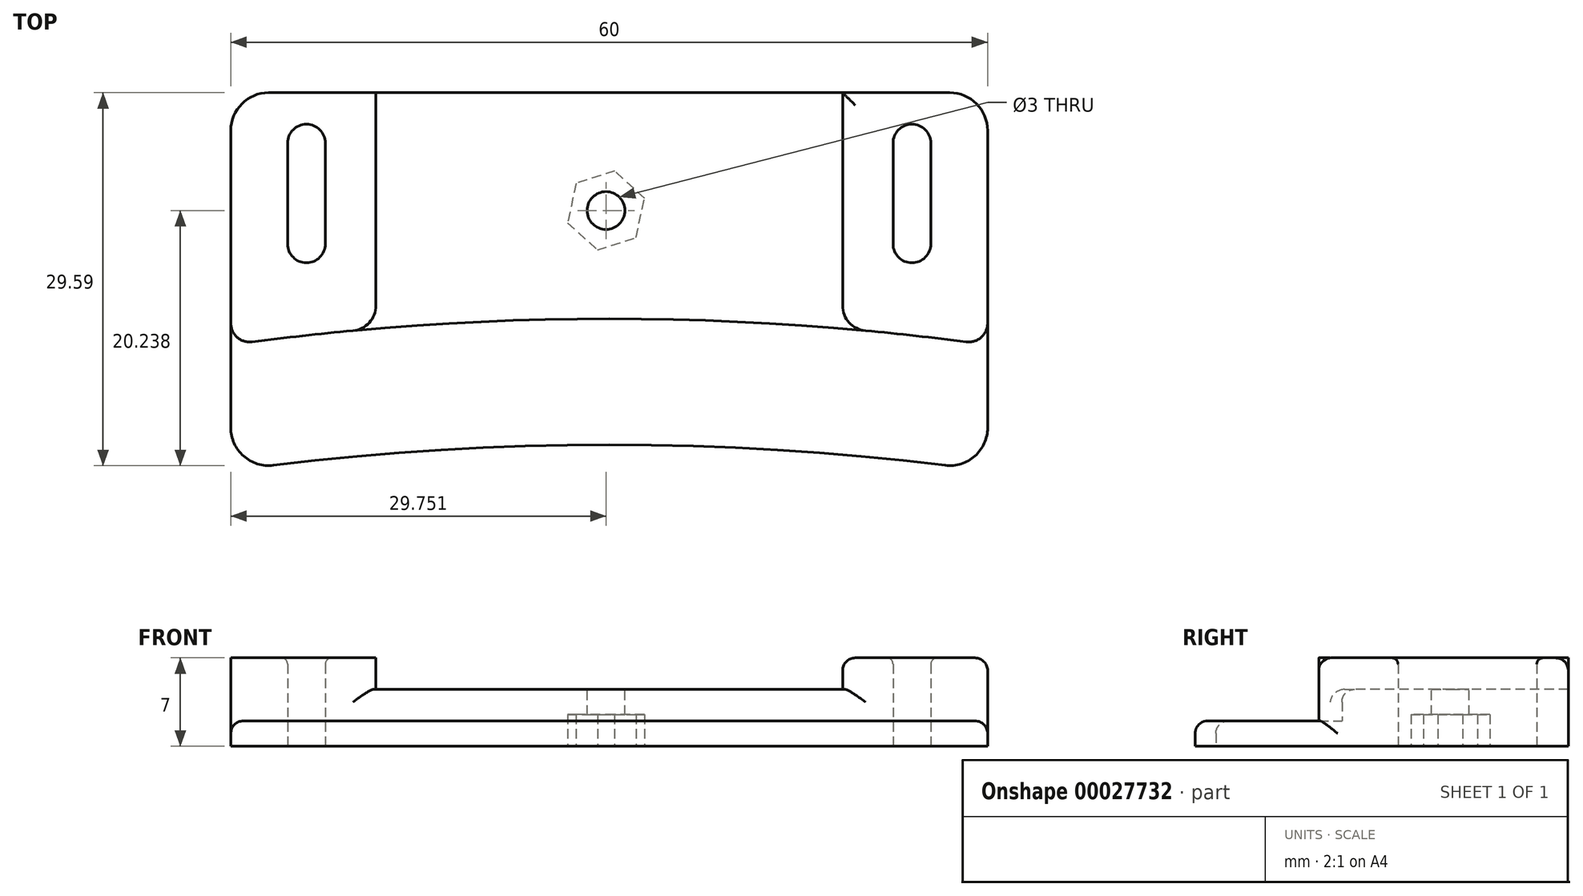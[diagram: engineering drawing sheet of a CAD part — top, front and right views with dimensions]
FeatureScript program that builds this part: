
annotation { "Feature Type Name" : "Feature", "Feature Type Description" : "" }
export const myFeature = defineFeature(function(context is Context, id is Id, definition is map)
    precondition{}
    {
        {
            var Q0;
            Q0=qCreatedBy(makeId("Top.planeOp"),FACE);
            var sketch = newSketch(context, id + "F0", { "sketchPlane" : qUnion([Q0])});
            skLineSegment(sketch, "E0.bottom", {"start": v(-20.27, 13.5) * mm, "end": v(33.73, 13.5) * mm});
            skLineSegment(sketch, "E0.left", {"start": v(-23.27, 10.5) * mm, "end": v(-23.27, -13.09) * mm});
            skLineSegment(sketch, "E0.right", {"start": v(36.73, 10.5) * mm, "end": v(36.73, -13.09) * mm});
            skLineSegment(sketch, "E1.bottom", {"start": v(-17.27, 11) * mm, "end": v(-17.27, 11) * mm});
            skLineSegment(sketch, "E1.top", {"start": v(-17.27, 0) * mm, "end": v(-17.27, 0) * mm});
            skLineSegment(sketch, "E1.left", {"start": v(-18.77, 9.5) * mm, "end": v(-18.77, 1.5) * mm});
            skLineSegment(sketch, "E1.right", {"start": v(-15.77, 9.5) * mm, "end": v(-15.77, 1.5) * mm});
            skLineSegment(sketch, "E2.bottom", {"start": v(30.73, 11) * mm, "end": v(30.73, 11) * mm});
            skLineSegment(sketch, "E2.top", {"start": v(30.73, 0) * mm, "end": v(30.73, 0) * mm});
            skLineSegment(sketch, "E2.left", {"start": v(29.23, 9.5) * mm, "end": v(29.23, 1.5) * mm});
            skLineSegment(sketch, "E2.right", {"start": v(32.23, 9.5) * mm, "end": v(32.23, 1.5) * mm});
            skArc(sketch, "E3", {"start": v(33.37, -16.06) * mm, "mid": v(6.73, -14.44) * mm, "end": v(-19.9, -16.06) * mm});
            skPoint(sketch, "E4.visualSharp", {"position": v(-23.27, 13.5) * mm});
            skArc(sketch, "E4.filletArc", {"start": v(-20.27, 13.5) * mm, "mid": v(-22.4, 12.62) * mm, "end": v(-23.27, 10.5) * mm});
            skPoint(sketch, "E5.visualSharp", {"position": v(-23.27, -16.5) * mm});
            skArc(sketch, "E5.filletArc", {"start": v(-23.27, -13.09) * mm, "mid": v(-22.26, -15.33) * mm, "end": v(-19.9, -16.06) * mm});
            skPoint(sketch, "E6.visualSharp", {"position": v(36.73, -16.5) * mm});
            skArc(sketch, "E6.filletArc", {"start": v(33.37, -16.06) * mm, "mid": v(35.72, -15.33) * mm, "end": v(36.73, -13.09) * mm});
            skPoint(sketch, "E7.visualSharp", {"position": v(36.73, 13.5) * mm});
            skArc(sketch, "E7.filletArc", {"start": v(36.73, 10.5) * mm, "mid": v(35.85, 12.62) * mm, "end": v(33.73, 13.5) * mm});
            skPoint(sketch, "E8.visualSharp", {"position": v(-18.77, 11) * mm});
            skArc(sketch, "E8.filletArc", {"start": v(-17.27, 11) * mm, "mid": v(-18.33, 10.56) * mm, "end": v(-18.77, 9.5) * mm});
            skPoint(sketch, "E9.visualSharp", {"position": v(-15.77, 11) * mm});
            skArc(sketch, "E9.filletArc", {"start": v(-15.77, 9.5) * mm, "mid": v(-16.2, 10.56) * mm, "end": v(-17.27, 11) * mm});
            skPoint(sketch, "E10.visualSharp", {"position": v(-18.77, 0) * mm});
            skArc(sketch, "E10.filletArc", {"start": v(-18.77, 1.5) * mm, "mid": v(-18.33, 0.44) * mm, "end": v(-17.27, 0) * mm});
            skPoint(sketch, "E11.visualSharp", {"position": v(-15.77, 0) * mm});
            skArc(sketch, "E11.filletArc", {"start": v(-17.27, 0) * mm, "mid": v(-16.2, 0.44) * mm, "end": v(-15.77, 1.5) * mm});
            skPoint(sketch, "E12.visualSharp", {"position": v(29.23, 0) * mm});
            skArc(sketch, "E12.filletArc", {"start": v(29.23, 1.5) * mm, "mid": v(29.67, 0.44) * mm, "end": v(30.73, 0) * mm});
            skPoint(sketch, "E13.visualSharp", {"position": v(32.23, 0) * mm});
            skArc(sketch, "E13.filletArc", {"start": v(30.73, 0) * mm, "mid": v(31.8, 0.44) * mm, "end": v(32.23, 1.5) * mm});
            skPoint(sketch, "E14.visualSharp", {"position": v(29.23, 11) * mm});
            skArc(sketch, "E14.filletArc", {"start": v(30.73, 11) * mm, "mid": v(29.67, 10.56) * mm, "end": v(29.23, 9.5) * mm});
            skPoint(sketch, "E15.visualSharp", {"position": v(32.23, 11) * mm});
            skArc(sketch, "E15.filletArc", {"start": v(32.23, 9.5) * mm, "mid": v(31.8, 10.56) * mm, "end": v(30.73, 11) * mm});
            skSolve(sketch);
        }
        {
            var Q0;
            Q0 = qSketchRegion(id + "F0", true);
            extrude(context, id + "F1", {"entities" : qUnion([Q0]), "depth" : 2 * mm});
        }
        {
            var Q0;
            Q0=makeQuery(id+"F1.opExtrude","CAP_FACE",FACE,{"disambiguationData":[OSD([sQuery(id+"F0.wireOp",EDGE,"E0.bottom"),sQuery(id+"F0.wireOp",EDGE,"E0.left"),sQuery(id+"F0.wireOp",EDGE,"E0.right"),sQuery(id+"F0.wireOp",EDGE,"E1.bottom"),sQuery(id+"F0.wireOp",EDGE,"E1.top"),sQuery(id+"F0.wireOp",EDGE,"E1.left"),sQuery(id+"F0.wireOp",EDGE,"E1.right"),sQuery(id+"F0.wireOp",EDGE,"E2.bottom"),sQuery(id+"F0.wireOp",EDGE,"E2.top"),sQuery(id+"F0.wireOp",EDGE,"E2.left"),sQuery(id+"F0.wireOp",EDGE,"E2.right"),sQuery(id+"F0.wireOp",EDGE,"E3"),sQuery(id+"F0.wireOp",EDGE,"E4.filletArc"),sQuery(id+"F0.wireOp",EDGE,"E5.filletArc"),sQuery(id+"F0.wireOp",EDGE,"E6.filletArc"),sQuery(id+"F0.wireOp",EDGE,"E7.filletArc"),sQuery(id+"F0.wireOp",EDGE,"E8.filletArc"),sQuery(id+"F0.wireOp",EDGE,"E9.filletArc"),sQuery(id+"F0.wireOp",EDGE,"E10.filletArc"),sQuery(id+"F0.wireOp",EDGE,"E11.filletArc"),sQuery(id+"F0.wireOp",EDGE,"E12.filletArc"),sQuery(id+"F0.wireOp",EDGE,"E13.filletArc"),sQuery(id+"F0.wireOp",EDGE,"E14.filletArc"),sQuery(id+"F0.wireOp",EDGE,"E15.filletArc")])],"isStart":false});
            var sketch = newSketch(context, id + "F2", { "sketchPlane" : qUnion([Q0])});
            skLineSegment(sketch, "E16", {"start": v(-23.27, -4.79) * mm, "end": v(-23.27, 10.5) * mm});
            skLineSegment(sketch, "E17", {"start": v(-20.27, 13.5) * mm, "end": v(33.73, 13.5) * mm});
            skLineSegment(sketch, "E18", {"start": v(36.73, 10.5) * mm, "end": v(36.73, -4.79) * mm});
            skArc(sketch, "E19", {"start": v(35.04, -6.27) * mm, "mid": v(6.73, -4.44) * mm, "end": v(-21.58, -6.27) * mm});
            skPoint(sketch, "E20.visualSharp", {"position": v(-23.27, -6.5) * mm});
            skArc(sketch, "E20.filletArc", {"start": v(-23.27, -4.79) * mm, "mid": v(-22.76, -5.91) * mm, "end": v(-21.58, -6.27) * mm});
            skPoint(sketch, "E21.visualSharp", {"position": v(36.73, -6.5) * mm});
            skArc(sketch, "E21.filletArc", {"start": v(35.04, -6.27) * mm, "mid": v(36.22, -5.91) * mm, "end": v(36.73, -4.79) * mm});
            skPoint(sketch, "E22.visualSharp", {"position": v(-23.27, 13.5) * mm});
            skArc(sketch, "E22.filletArc", {"start": v(-20.27, 13.5) * mm, "mid": v(-22.4, 12.62) * mm, "end": v(-23.27, 10.5) * mm});
            skPoint(sketch, "E23.visualSharp", {"position": v(36.73, 13.5) * mm});
            skArc(sketch, "E23.filletArc", {"start": v(36.73, 10.5) * mm, "mid": v(35.85, 12.62) * mm, "end": v(33.73, 13.5) * mm});
            skSolve(sketch);
        }
        {
            var Q0;
            Q0=makeQuery(id+"F2.imprint","IMPRINT",FACE,{"disambiguationData":[TD([[makeQuery(id+"F2.imprint","IMPRINT",EDGE,{"derivedFrom":sQuery(id+"F2.wireOp",EDGE,"E16")}),1.0]])]});
            extrude(context, id + "F3", {"entities" : qUnion([Q0]), "operationType" : NewBodyOperationType.ADD, "depth" : 5 * mm});
        }
        {
            var Q0;
            Q0=makeQuery(id+"F3.opExtrude","CAP_FACE",FACE,{"disambiguationData":[OSD([sQuery(id+"F0.wireOp",EDGE,"E1.bottom"),sQuery(id+"F0.wireOp",EDGE,"E1.top"),sQuery(id+"F0.wireOp",EDGE,"E1.left"),sQuery(id+"F0.wireOp",EDGE,"E1.right"),sQuery(id+"F0.wireOp",EDGE,"E2.bottom"),sQuery(id+"F0.wireOp",EDGE,"E2.top"),sQuery(id+"F0.wireOp",EDGE,"E2.left"),sQuery(id+"F0.wireOp",EDGE,"E2.right"),sQuery(id+"F0.wireOp",EDGE,"E8.filletArc"),sQuery(id+"F0.wireOp",EDGE,"E9.filletArc"),sQuery(id+"F0.wireOp",EDGE,"E10.filletArc"),sQuery(id+"F0.wireOp",EDGE,"E11.filletArc"),sQuery(id+"F0.wireOp",EDGE,"E12.filletArc"),sQuery(id+"F0.wireOp",EDGE,"E13.filletArc"),sQuery(id+"F0.wireOp",EDGE,"E14.filletArc"),sQuery(id+"F0.wireOp",EDGE,"E15.filletArc"),sQuery(id+"F2.wireOp",EDGE,"E16"),sQuery(id+"F2.wireOp",EDGE,"E17"),sQuery(id+"F2.wireOp",EDGE,"E18"),sQuery(id+"F2.wireOp",EDGE,"E19"),sQuery(id+"F2.wireOp",EDGE,"E20.filletArc"),sQuery(id+"F2.wireOp",EDGE,"E21.filletArc"),sQuery(id+"F2.wireOp",EDGE,"E22.filletArc"),sQuery(id+"F2.wireOp",EDGE,"E23.filletArc")])],"isStart":false});
            var sketch = newSketch(context, id + "F4", { "sketchPlane" : qUnion([Q0])});
            skLineSegment(sketch, "E24.bottom", {"start": v(-11.77, 13.5) * mm, "end": v(25.23, 13.5) * mm});
            skLineSegment(sketch, "E24.top", {"start": v(-11.77, -11.2) * mm, "end": v(25.23, -11.2) * mm});
            skLineSegment(sketch, "E24.left", {"start": v(-11.77, 13.5) * mm, "end": v(-11.77, -11.2) * mm});
            skLineSegment(sketch, "E24.right", {"start": v(25.23, 13.5) * mm, "end": v(25.23, -11.2) * mm});
            skSolve(sketch);
        }
        {
            var Q0;
            {var subQ6=sQuery(id+"F4.wireOp",EDGE,"E24.bottom");Q0=makeQuery(id+"F4.imprint","IMPRINT",FACE,{"disambiguationData":[TD([[makeQuery(id+"F4.imprint","IMPRINT",EDGE,{"derivedFrom":subQ6}),-1.0]])]});}
            var Q1;
            {var subQ5=sQuery(id+"F4.wireOp",EDGE,"E24.top");Q1=makeQuery(id+"F4.imprint","IMPRINT",FACE,{"disambiguationData":[TD([[makeQuery(id+"F4.imprint","IMPRINT",EDGE,{"derivedFrom":subQ5}),1.0]])]});}
            extrude(context, id + "F5", {"entities" : qUnion([Q0, Q1]), "operationType" : NewBodyOperationType.REMOVE, "oppositeDirection" : true, "depth" : 2.5 * mm});
        }
        {
            var Q0;
            Q0=makeQuery(id+"F5.boolean.opBoolean","COPY",FACE,{"derivedFrom":makeQuery(id+"F5.opExtrude","CAP_FACE",FACE,{"disambiguationData":[OSD([sQuery(id+"F4.wireOp",EDGE,"E24.bottom"),sQuery(id+"F4.wireOp",EDGE,"E24.top"),sQuery(id+"F4.wireOp",EDGE,"E24.left"),sQuery(id+"F4.wireOp",EDGE,"E24.right")])],"isStart":false})});
            var sketch = newSketch(context, id + "F6", { "sketchPlane" : qUnion([Q0])});
            skCircle(sketch, "E25", {"center": v(6.48, 4.15) * mm, "radius": 1.5 * mm});
            skSolve(sketch);
        }
        {
            var Q0;
            Q0 = qSketchRegion(id + "F6", true);
            extrude(context, id + "F7", {"entities" : qUnion([Q0]), "operationType" : NewBodyOperationType.REMOVE, "oppositeDirection" : true, "depth" : 25 * mm});
        }
        {
            var Q0;
            Q0=makeQuery(id+"F1.opExtrude","CAP_FACE",FACE,{"disambiguationData":[OSD([sQuery(id+"F0.wireOp",EDGE,"E0.bottom"),sQuery(id+"F0.wireOp",EDGE,"E0.left"),sQuery(id+"F0.wireOp",EDGE,"E0.right"),sQuery(id+"F0.wireOp",EDGE,"E1.bottom"),sQuery(id+"F0.wireOp",EDGE,"E1.top"),sQuery(id+"F0.wireOp",EDGE,"E1.left"),sQuery(id+"F0.wireOp",EDGE,"E1.right"),sQuery(id+"F0.wireOp",EDGE,"E2.bottom"),sQuery(id+"F0.wireOp",EDGE,"E2.top"),sQuery(id+"F0.wireOp",EDGE,"E2.left"),sQuery(id+"F0.wireOp",EDGE,"E2.right"),sQuery(id+"F0.wireOp",EDGE,"E3"),sQuery(id+"F0.wireOp",EDGE,"E4.filletArc"),sQuery(id+"F0.wireOp",EDGE,"E5.filletArc"),sQuery(id+"F0.wireOp",EDGE,"E6.filletArc"),sQuery(id+"F0.wireOp",EDGE,"E7.filletArc"),sQuery(id+"F0.wireOp",EDGE,"E8.filletArc"),sQuery(id+"F0.wireOp",EDGE,"E9.filletArc"),sQuery(id+"F0.wireOp",EDGE,"E10.filletArc"),sQuery(id+"F0.wireOp",EDGE,"E11.filletArc"),sQuery(id+"F0.wireOp",EDGE,"E12.filletArc"),sQuery(id+"F0.wireOp",EDGE,"E13.filletArc"),sQuery(id+"F0.wireOp",EDGE,"E14.filletArc"),sQuery(id+"F0.wireOp",EDGE,"E15.filletArc")])],"isStart":true});
            var sketch = newSketch(context, id + "F8", { "sketchPlane" : qUnion([Q0])});
            skCircle(sketch, "E26.cCircle", {"center": v(6.48, -4.15) * mm, "radius": 3.2 * mm, "construction": true});
            skLineSegment(sketch, "E26.0", {"start": v(9.53, -5.13) * mm, "end": v(7.15, -7.28) * mm});
            skLineSegment(sketch, "E26.1", {"start": v(7.15, -7.28) * mm, "end": v(4.1, -6.3) * mm});
            skLineSegment(sketch, "E26.2", {"start": v(4.1, -6.3) * mm, "end": v(3.43, -3.17) * mm});
            skLineSegment(sketch, "E26.3", {"start": v(3.43, -3.17) * mm, "end": v(5.8, -1.02) * mm});
            skLineSegment(sketch, "E26.4", {"start": v(5.8, -1.02) * mm, "end": v(8.86, -2) * mm});
            skLineSegment(sketch, "E26.5", {"start": v(8.86, -2) * mm, "end": v(9.53, -5.13) * mm});
            skSolve(sketch);
        }
        {
            var Q0;
            Q0 = qSketchRegion(id + "F8", true);
            extrude(context, id + "F9", {"entities" : qUnion([Q0]), "operationType" : NewBodyOperationType.REMOVE, "oppositeDirection" : true, "depth" : 2.5 * mm});
        }
        {
            var Q0;
            Q0=makeQuery(id+"F5.boolean.opBoolean","INTERSECT",EDGE,{"derivedFrom":[makeQuery(id+"F3.opExtrude","SWEPT_FACE",FACE,{"disambiguationData":[OSD([sQuery(id+"F2.wireOp",EDGE,"E19")])]}),makeQuery(id+"F5.opExtrude","SWEPT_FACE",FACE,{"disambiguationData":[OSD([sQuery(id+"F4.wireOp",EDGE,"E24.right")])]})]});
            var Q1;
            Q1=makeQuery(id+"F5.boolean.opBoolean","INTERSECT",EDGE,{"derivedFrom":[makeQuery(id+"F3.opExtrude","SWEPT_FACE",FACE,{"disambiguationData":[OSD([sQuery(id+"F2.wireOp",EDGE,"E19")])]}),makeQuery(id+"F5.opExtrude","SWEPT_FACE",FACE,{"disambiguationData":[OSD([sQuery(id+"F4.wireOp",EDGE,"E24.left")])]})]});
            var Q2;
            Q2=makeQuery(id+"F5.boolean.opBoolean","COPY",EDGE,{"derivedFrom":makeQuery(id+"F5.opExtrude","SWEPT_EDGE",EDGE,{"disambiguationData":[OSD([sQuery(id+"F2.wireOp",EDGE,"E17"),sQuery(id+"F4.wireOp",EDGE,"E24.bottom"),sQuery(id+"F4.wireOp",EDGE,"E24.left")])]})});
            var Q3;
            Q3=makeQuery(id+"F5.boolean.opBoolean","COPY",EDGE,{"derivedFrom":makeQuery(id+"F5.opExtrude","SWEPT_EDGE",EDGE,{"disambiguationData":[OSD([sQuery(id+"F2.wireOp",EDGE,"E17"),sQuery(id+"F4.wireOp",EDGE,"E24.bottom"),sQuery(id+"F4.wireOp",EDGE,"E24.right")])]})});
            fillet(context, id + "F10", {"entities" : qUnion([Q0, Q1, Q2, Q3]), "radius" : 2 * mm, "tangentPropagation" : true, "allowEdgeOverflow" : false});
        }
        {
            var Q0;
            Q0=makeQuery(id+"F5.boolean.opBoolean","COPY",EDGE,{"derivedFrom":makeQuery(id+"F5.opExtrude","CAP_EDGE",EDGE,{"disambiguationData":[OSD([sQuery(id+"F4.wireOp",EDGE,"E24.left")])],"isStart":true})});
            var Q1;
            Q1=makeQuery(id+"F3.opExtrude","CAP_EDGE",EDGE,{"disambiguationData":[OSD([sQuery(id+"F2.wireOp",EDGE,"E18")])],"isStart":false});
            var Q2;
            Q2=makeQuery(id+"F1.opExtrude","CAP_EDGE",EDGE,{"disambiguationData":[OSD([sQuery(id+"F0.wireOp",EDGE,"E3")])],"isStart":false});
            var Q3;
            Q3=makeQuery(id+"F5.boolean.opBoolean","INTERSECT",EDGE,{"derivedFrom":[makeQuery(id+"F3.opExtrude","SWEPT_FACE",FACE,{"disambiguationData":[OSD([sQuery(id+"F2.wireOp",EDGE,"E19")])]}),makeQuery(id+"F5.opExtrude","CAP_FACE",FACE,{"disambiguationData":[OSD([sQuery(id+"F4.wireOp",EDGE,"E24.bottom"),sQuery(id+"F4.wireOp",EDGE,"E24.top"),sQuery(id+"F4.wireOp",EDGE,"E24.left"),sQuery(id+"F4.wireOp",EDGE,"E24.right")])],"isStart":false})]});
            var Q4;
            Q4=makeQuery(id+"F5.boolean.opBoolean","COPY",EDGE,{"derivedFrom":makeQuery(id+"F5.opExtrude","CAP_EDGE",EDGE,{"disambiguationData":[OSD([sQuery(id+"F4.wireOp",EDGE,"E24.bottom")])],"isStart":false})});
            fillet(context, id + "F11", {"entities" : qUnion([Q0, Q1, Q2, Q3, Q4]), "radius" : 1 * mm, "tangentPropagation" : true, "allowEdgeOverflow" : false});
        }
        {
            var Q0;
            Q0=makeQuery(id+"F7.boolean.opBoolean","COPY",EDGE,{"derivedFrom":makeQuery(id+"F7.opExtrude","CAP_EDGE",EDGE,{"disambiguationData":[OSD([sQuery(id+"F6.wireOp",EDGE,"E25")])],"isStart":true})});
            var Q1;
            Q1=makeQuery(id+"F3.opExtrude","CAP_EDGE",EDGE,{"disambiguationData":[OSD([sQuery(id+"F0.wireOp",EDGE,"E2.left")])],"isStart":false});
            var Q2;
            Q2=makeQuery(id+"F3.opExtrude","CAP_EDGE",EDGE,{"disambiguationData":[OSD([sQuery(id+"F0.wireOp",EDGE,"E1.right")])],"isStart":false});
            fillet(context, id + "F12", {"entities" : qUnion([Q0, Q1, Q2]), "radius" : 0.5 * mm, "tangentPropagation" : true, "allowEdgeOverflow" : false});
        }
    });
